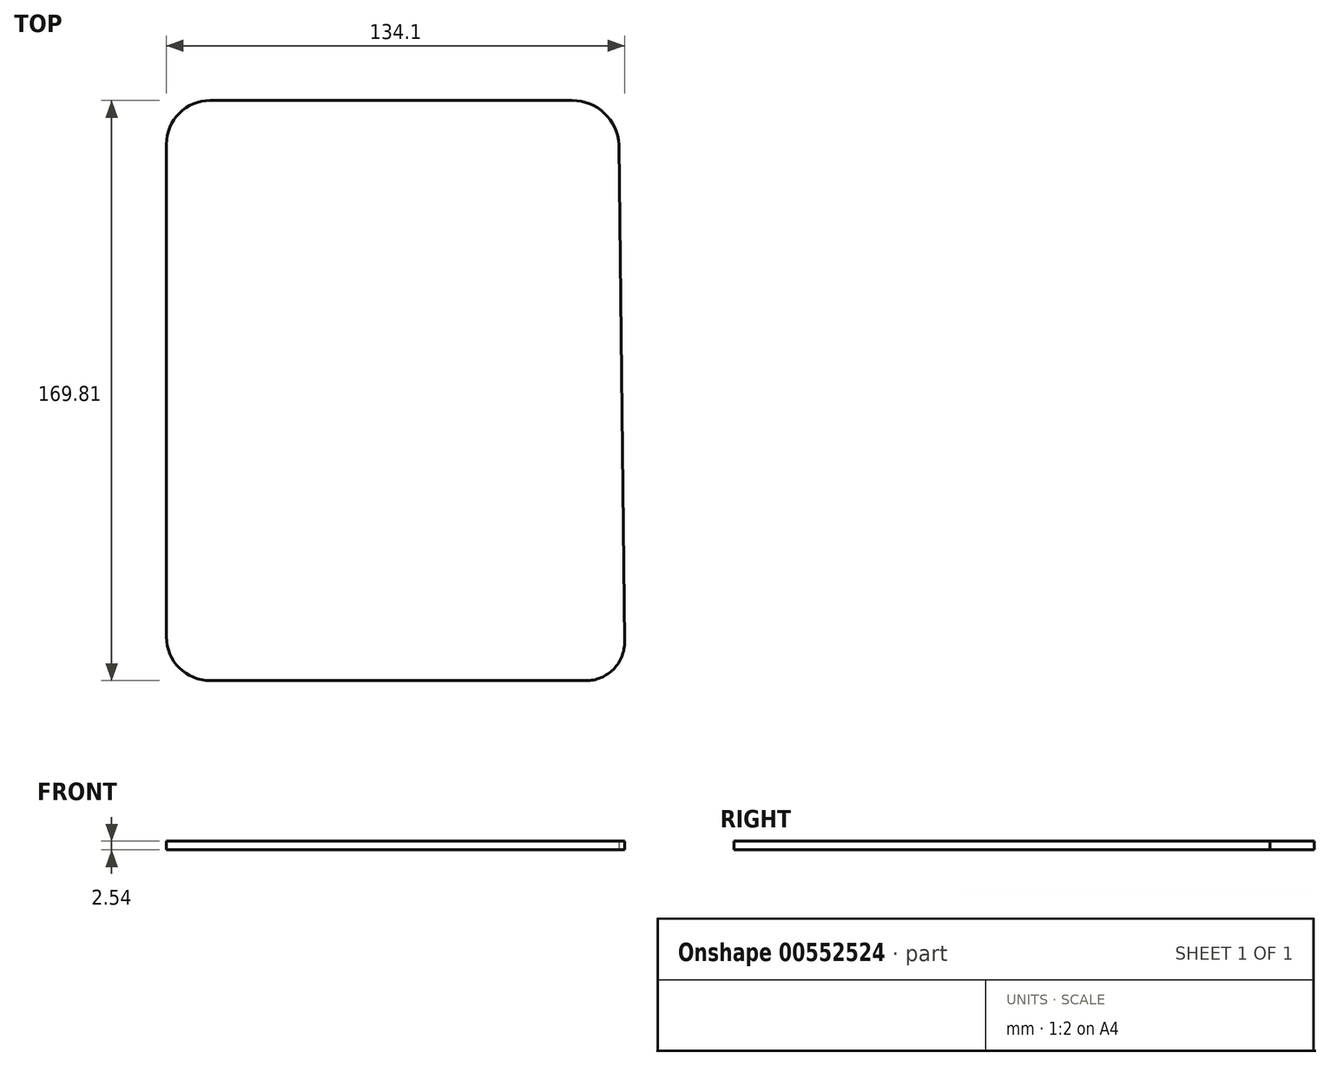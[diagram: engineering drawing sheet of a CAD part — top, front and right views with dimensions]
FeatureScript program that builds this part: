
annotation { "Feature Type Name" : "Feature", "Feature Type Description" : "" }
export const myFeature = defineFeature(function(context is Context, id is Id, definition is map)
    precondition{}
    {
        {
            var Q0;
            Q0=qCreatedBy(makeId("Top.planeOp"),FACE);
            var sketch = newSketch(context, id + "F0", { "sketchPlane" : qUnion([Q0])});
            skLineSegment(sketch, "E0", {"start": v(105.92, 0) * mm, "end": v(0, 0) * mm});
            skArc(sketch, "E1", {"start": v(105.92, 0) * mm, "mid": v(115.34, -3.76) * mm, "end": v(119.6, -12.97) * mm});
            skArc(sketch, "E2", {"start": v(0, 0) * mm, "mid": v(-9.08, -3.76) * mm, "end": v(-12.84, -12.84) * mm});
            skLineSegment(sketch, "E3", {"start": v(-12.84, -156.98) * mm, "end": v(-12.84, -12.84) * mm});
            skArc(sketch, "E4", {"start": v(-12.84, -156.98) * mm, "mid": v(-9.08, -166.05) * mm, "end": v(0, -169.81) * mm});
            skLineSegment(sketch, "E5", {"start": v(110, -169.81) * mm, "end": v(0, -169.81) * mm});
            skArc(sketch, "E6", {"start": v(110, -169.81) * mm, "mid": v(118.04, -166.44) * mm, "end": v(121.26, -158.34) * mm});
            skLineSegment(sketch, "E7", {"start": v(121.26, -158.34) * mm, "end": v(119.6, -12.97) * mm});
            skSolve(sketch);
        }
        {
            var Q0;
            Q0=makeQuery(id+"F0.imprint","IMPRINT",FACE,{"disambiguationData":[TD([[makeQuery(id+"F0.imprint","IMPRINT",EDGE,{"derivedFrom":sQuery(id+"F0.wireOp",EDGE,"E0")}),1.0]])]});
            extrude(context, id + "F1", {"entities" : qUnion([Q0]), "depth" : 2.54 * mm, "offsetDistance" : 25.4 * mm});
        }
    });
